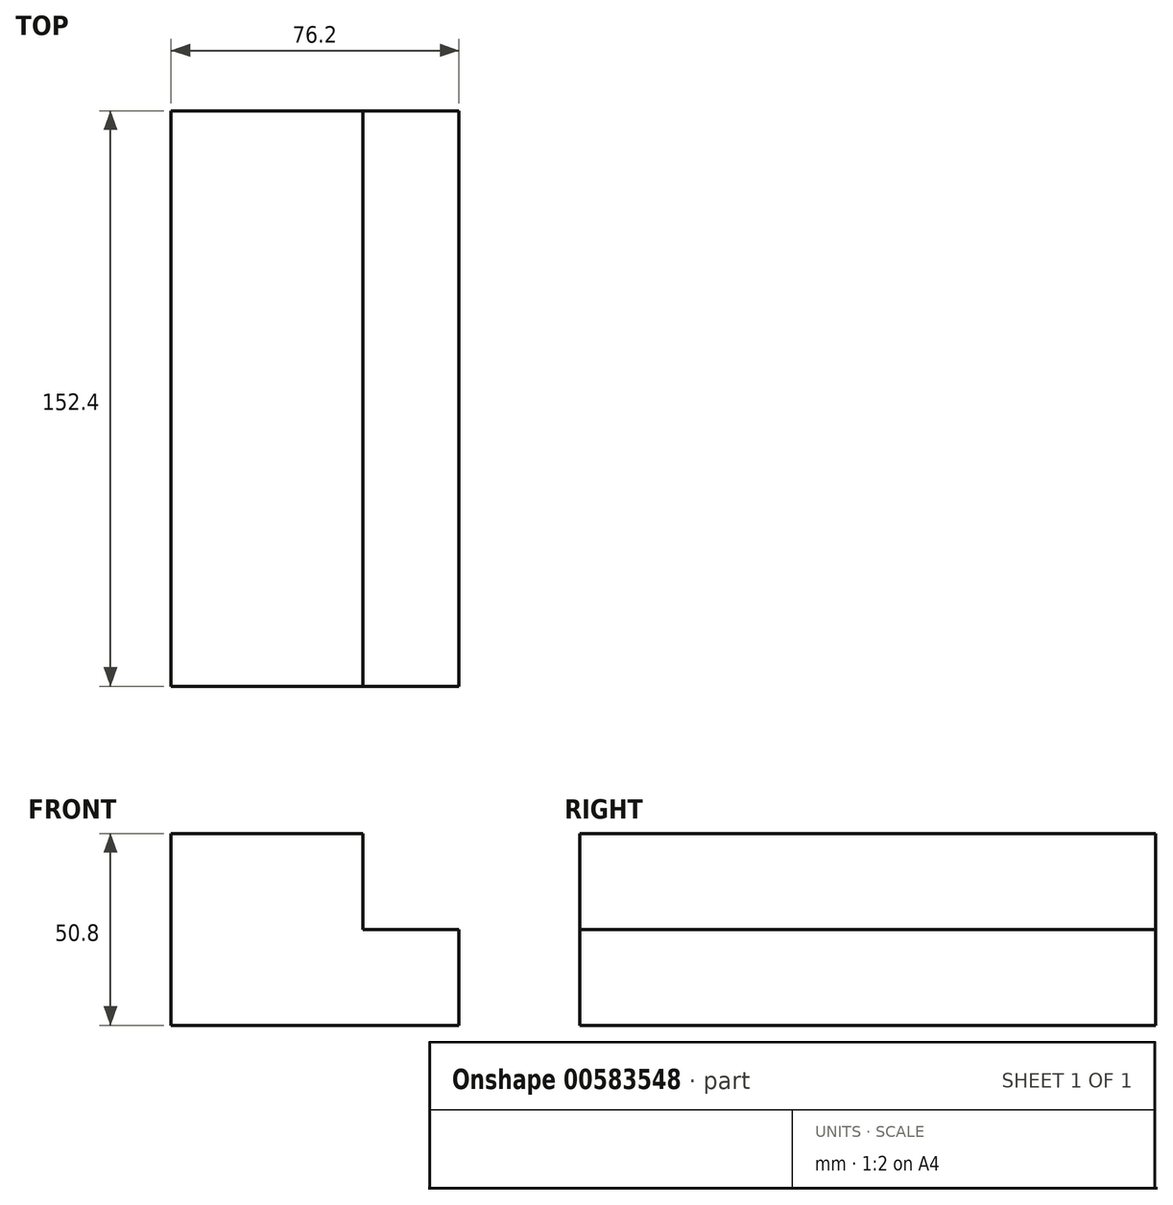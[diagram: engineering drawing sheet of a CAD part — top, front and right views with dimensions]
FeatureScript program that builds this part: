
annotation { "Feature Type Name" : "Feature", "Feature Type Description" : "" }
export const myFeature = defineFeature(function(context is Context, id is Id, definition is map)
    precondition{}
    {
        {
            var Q0;
            Q0=qCreatedBy(makeId("Front.planeOp"),FACE);
            var sketch = newSketch(context, id + "F0", { "sketchPlane" : qUnion([Q0])});
            skLineSegment(sketch, "E0", {"start": v(0, 0) * mm, "end": v(76.2, 0) * mm});
            skLineSegment(sketch, "E1", {"start": v(0, 0) * mm, "end": v(0, 50.8) * mm});
            skLineSegment(sketch, "E2", {"start": v(0, 50.8) * mm, "end": v(50.8, 50.8) * mm});
            skLineSegment(sketch, "E3", {"start": v(50.8, 50.8) * mm, "end": v(50.8, 25.4) * mm});
            skLineSegment(sketch, "E4", {"start": v(50.8, 25.4) * mm, "end": v(76.2, 25.4) * mm});
            skLineSegment(sketch, "E5", {"start": v(76.2, 25.4) * mm, "end": v(76.2, 0) * mm});
            skSolve(sketch);
        }
        {
            var Q0;
            Q0 = qSketchRegion(id + "F0", true);
            extrude(context, id + "F1", {"entities" : qUnion([Q0]), "depth" : 152.4 * mm, "offsetDistance" : 25.4 * mm});
        }
    });
